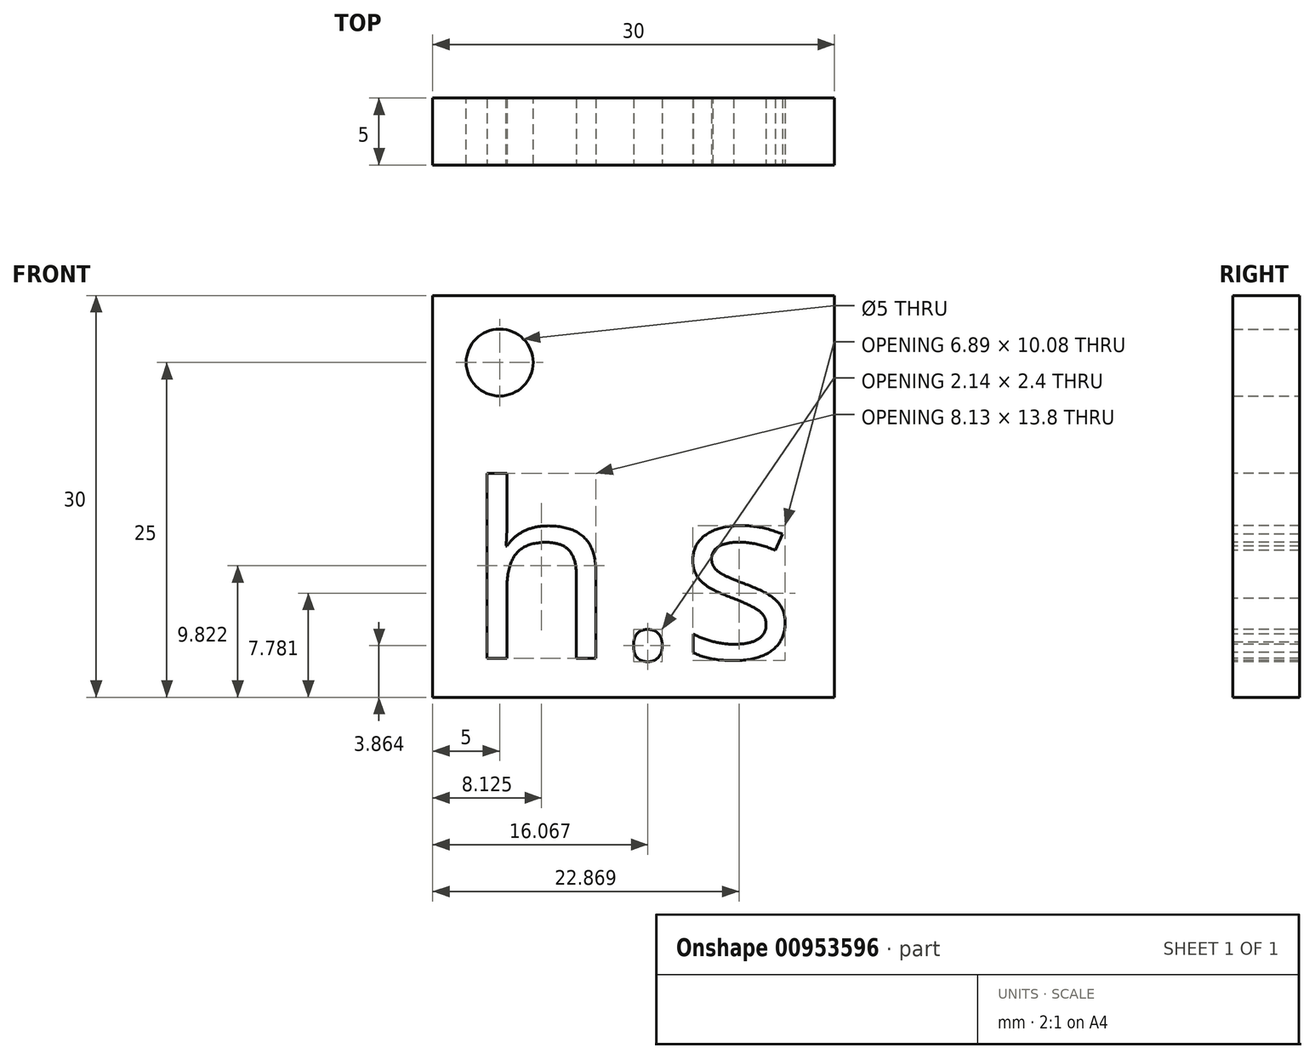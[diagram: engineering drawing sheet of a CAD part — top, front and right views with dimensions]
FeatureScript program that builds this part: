
annotation { "Feature Type Name" : "Feature", "Feature Type Description" : "" }
export const myFeature = defineFeature(function(context is Context, id is Id, definition is map)
    precondition{}
    {
        {
            var Q0;
            Q0=qCreatedBy(makeId("Front.planeOp"),FACE);
            var sketch = newSketch(context, id + "F0", { "sketchPlane" : qUnion([Q0])});
            skLineSegment(sketch, "E0.bottom", {"start": v(0, 0) * mm, "end": v(30, 0) * mm});
            skLineSegment(sketch, "E0.top", {"start": v(0, 30) * mm, "end": v(30, 30) * mm});
            skLineSegment(sketch, "E0.left", {"start": v(0, 0) * mm, "end": v(0, 30) * mm});
            skLineSegment(sketch, "E0.right", {"start": v(30, 0) * mm, "end": v(30, 30) * mm});
            skCircle(sketch, "E1", {"center": v(5, 25) * mm, "radius": 2.5 * mm});
            skSolve(sketch);
        }
        {
            var Q0;
            Q0 = qSketchRegion(id + "FAVhYDEPnWWRPO1_0", true);
            var Q1;
            Q1 = qSketchRegion(id + "F0", true);
            var Q2;
            Q2 = qSketchRegion(id + "F2", true);
            extrude(context, id + "F1", {"entities" : qUnion([Q0, Q1, Q2]), "depth" : 5 * mm, "offsetDistance" : 25 * mm});
        }
        {
            var Q0;
            Q0=makeQuery(id+"F1.opExtrude","CAP_FACE",FACE,{"disambiguationData":[OSD([sQuery(id+"F0.wireOp",EDGE,"E0.bottom"),sQuery(id+"F0.wireOp",EDGE,"E0.top"),sQuery(id+"F0.wireOp",EDGE,"E0.left"),sQuery(id+"F0.wireOp",EDGE,"E0.right"),sQuery(id+"F0.wireOp",EDGE,"E1")])],"isStart":false});
            var sketch = newSketch(context, id + "F2", { "sketchPlane" : qUnion([Q0])});
            skText(sketch, "E2", { "text": "h.s\n", "fontName": "OpenSans-Regular.ttf"});
            const initialGuessF2  = {"E2": [0.0025, 0.00292, 1, 0, 0.01308]};
            skSetInitialGuess(sketch, initialGuessF2);
            skSolve(sketch);
        }
        {
            var Q0;
            Q0 = qSketchRegion(id + "F2", true);
            extrude(context, id + "F3", {"entities" : qUnion([Q0]), "operationType" : NewBodyOperationType.REMOVE, "endBound" : BoundingType.THROUGH_ALL, "oppositeDirection" : true, "depth" : 25 * mm, "offsetDistance" : 25 * mm});
        }
    });
